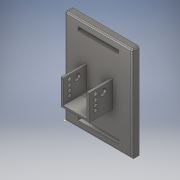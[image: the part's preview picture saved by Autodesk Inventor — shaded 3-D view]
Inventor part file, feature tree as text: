
AUTODESK INVENTOR PART (.ipt)
format: ipt  version: 2018 (Build 220112000, 112)  size: 206,848 bytes
history: native  units: in
note: dims shown in document units (in); Inventor stores cm internally (conversion verified against a paired STEP export)
features: extrude x9, sketch x8, fillet x1
ambient origin geometry x8: Origin, YZ Plane, XZ Plane, XY Plane, X Axis, Y Axis, Z Axis, Center Point
bodies: Solid1 (feature_tree)
feature tree (18):
  extrude  "Extrusion1"  Depth=7.0in
  sketch  "Sketch2"  dims[d2=0.5in d3=0.0in d6=1.75in d7=0.0in]
  sketch  "Sketch3"  dims[d8=10.0in d9=0.0in d10=0.25in]
  extrude  "Extrusion2"  Depth=1.75in TaperAngle=0.0deg
  sketch  "Sketch5"  dims[d17=1.35in d18=0.0in d19=1.35in d20=0.0in]
  extrude  "Extrusion3"  Depth=0.25in
  extrude  "Extrusion5"  Depth=1.35in TaperAngle=0.0deg
  extrude  "Extrusion6"  Depth=1.35in TaperAngle=0.0deg
  sketch  "Sketch7"  dims[d27=1.0in d28=0.0in d29=0.75in]
  extrude  "Extrusion7"  Depth=0.25in
  extrude  "Extrusion8"  Depth=0.75in
  extrude  "Extrusion11"  Depth=0.125in
  extrude  "Extrusion12"  Depth=0.125in
  fillet  "Fillet1"  Radius=0.45in
  sketch  "Sketch1"  dims[d0=5.0in d1=7.0in]
  sketch  "Sketch4"  dims[d13=10.0in d14=0.0in d15=1.35in d16=0.0in]
  sketch  "Sketch6"  dims[d25=0.25in d26=0.25in]
  sketch  "Sketch8"  dims[d30=0.45in d31=0.45in d32=0.45in d33=0.45in d34=0.45in d35=1.75in d36=0.0in d37=0.125in]
